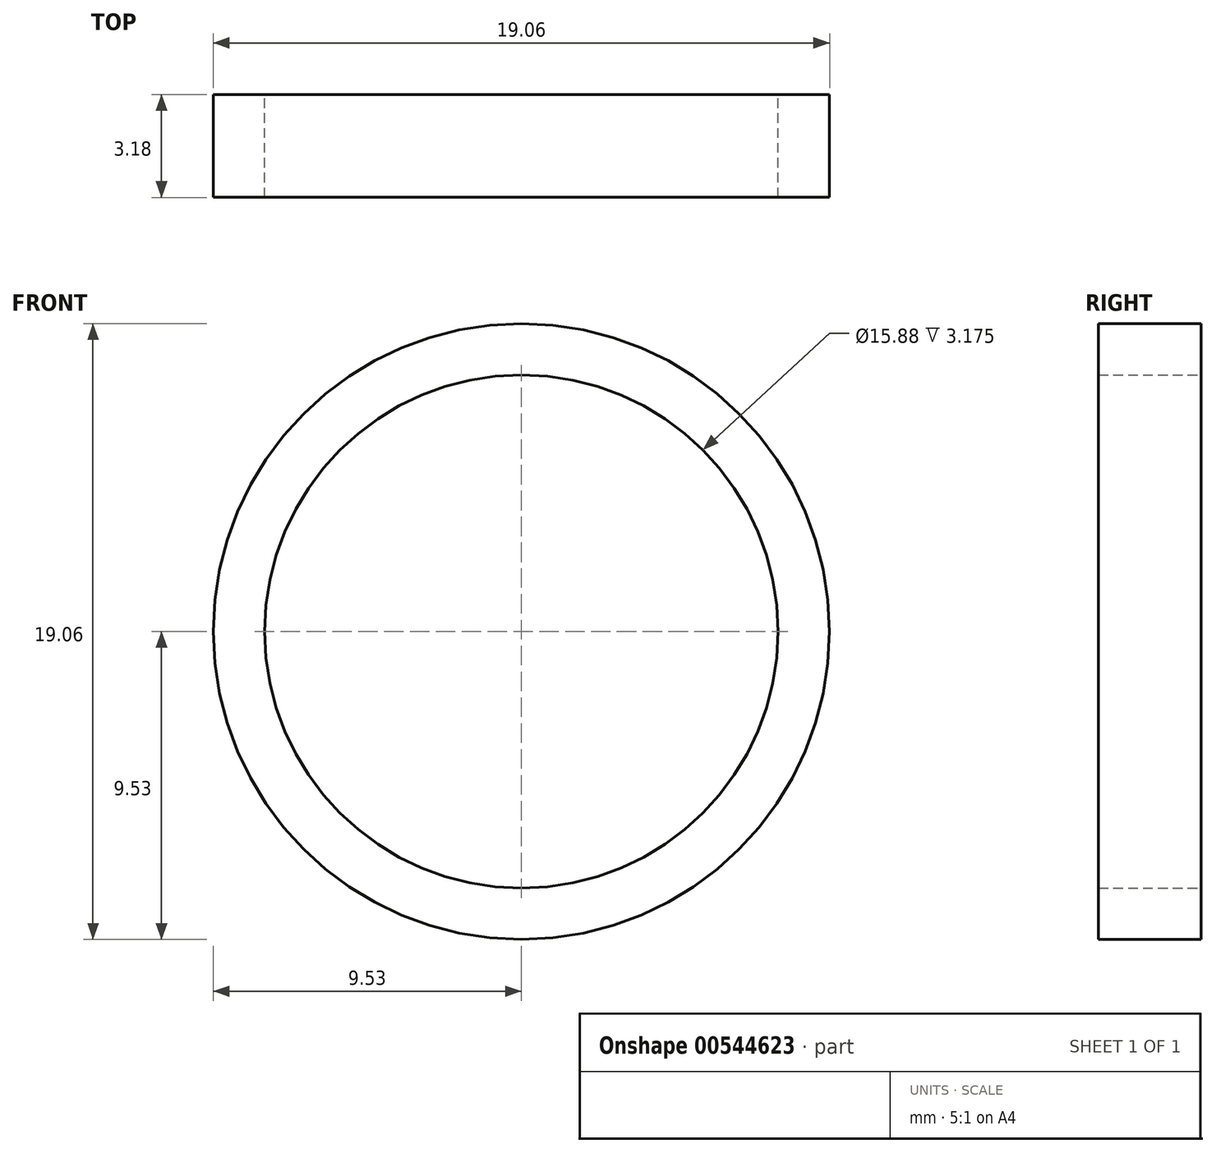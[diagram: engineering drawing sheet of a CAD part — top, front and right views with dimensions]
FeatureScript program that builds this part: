
annotation { "Feature Type Name" : "Feature", "Feature Type Description" : "" }
export const myFeature = defineFeature(function(context is Context, id is Id, definition is map)
    precondition{}
    {
        {
            var Q0;
            Q0=qCreatedBy(makeId("Front.planeOp"),FACE);
            var sketch = newSketch(context, id + "F0", { "sketchPlane" : qUnion([Q0])});
            skCircle(sketch, "E0", {"center": v(0, 0) * mm, "radius": 9.53 * mm});
            skCircle(sketch, "E1", {"center": v(0, 0) * mm, "radius": 7.94 * mm});
            skSolve(sketch);
        }
        {
            var Q0;
            Q0 = qSketchRegion(id + "F0", true);
            extrude(context, id + "F1", {"entities" : qUnion([Q0]), "depth" : 3.17 * mm, "offsetDistance" : 25.4 * mm});
        }
    });
